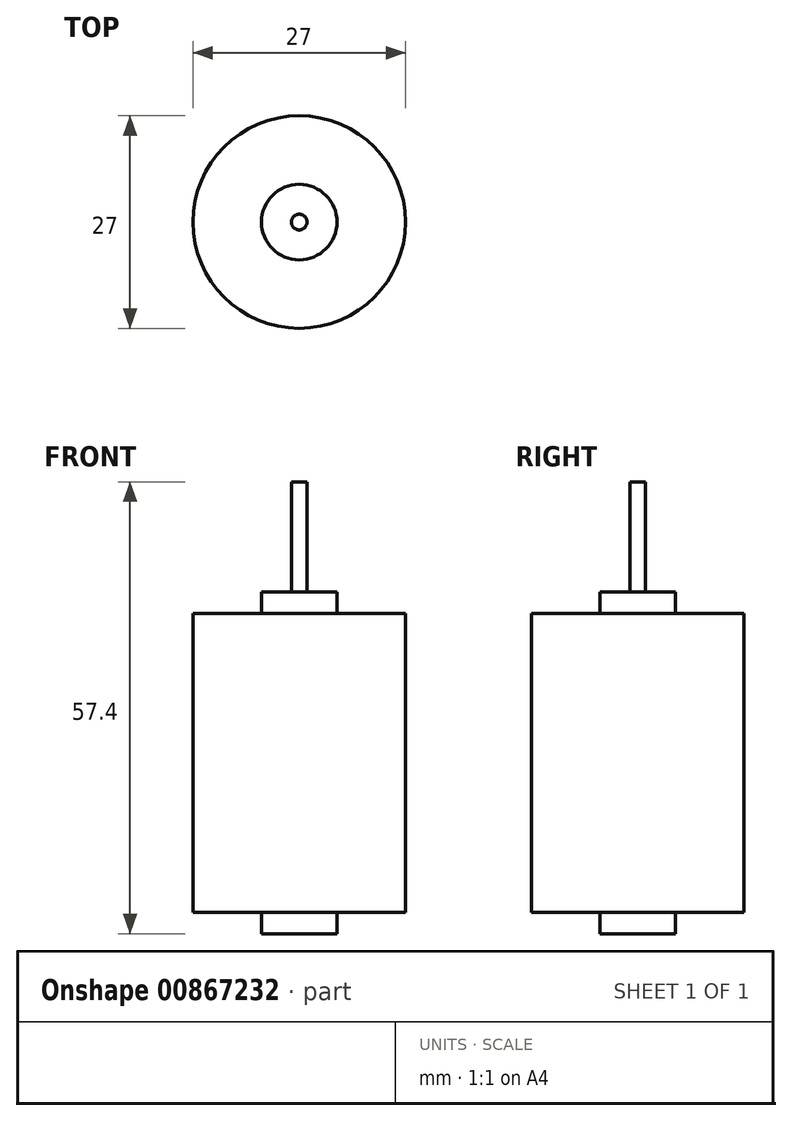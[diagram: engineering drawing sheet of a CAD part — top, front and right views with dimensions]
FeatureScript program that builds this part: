
annotation { "Feature Type Name" : "Feature", "Feature Type Description" : "" }
export const myFeature = defineFeature(function(context is Context, id is Id, definition is map)
    precondition{}
    {
        {
            var Q0;
            Q0=qCreatedBy(makeId("Right.planeOp"),FACE);
            var sketch = newSketch(context, id + "F0", { "sketchPlane" : qUnion([Q0])});
            skLineSegment(sketch, "E0", {"start": v(-56.5, 39.4) * mm, "end": v(-56.5, -18.04) * mm});
            skLineSegment(sketch, "E1", {"start": v(-56.5, 39.4) * mm, "end": v(-55.5, 39.4) * mm});
            skLineSegment(sketch, "E2", {"start": v(-55.5, 39.4) * mm, "end": v(-55.5, 25.4) * mm});
            skLineSegment(sketch, "E3", {"start": v(-55.5, 25.4) * mm, "end": v(-51.7, 25.4) * mm});
            skLineSegment(sketch, "E4", {"start": v(-51.7, 25.4) * mm, "end": v(-51.7, 22.7) * mm});
            skLineSegment(sketch, "E5", {"start": v(-51.7, 22.7) * mm, "end": v(-43, 22.7) * mm});
            skLineSegment(sketch, "E6", {"start": v(-43, 22.7) * mm, "end": v(-43, -15.3) * mm});
            skLineSegment(sketch, "E7", {"start": v(-43, -15.3) * mm, "end": v(-51.7, -15.3) * mm});
            skLineSegment(sketch, "E8", {"start": v(-51.7, -15.3) * mm, "end": v(-51.7, -18) * mm});
            skLineSegment(sketch, "E9", {"start": v(-51.7, -18) * mm, "end": v(-56.5, -18) * mm});
            skSolve(sketch);
        }
        {
            var Q0;
            {var subQ0=sQuery(id+"F0.wireOp",EDGE,"E1");Q0=makeQuery(id+"F0.imprint","IMPRINT",FACE,{"disambiguationData":[TD([[makeQuery(id+"F0.imprint","IMPRINT",EDGE,{"derivedFrom":subQ0}),-1.0]])]});}
            var Q1;
            Q1=sQuery(id+"F0.wireOp",EDGE,"E0");
            revolve(context, id + "F1", {"surfaceOperationType" : NewSurfaceOperationType.NEW, "entities" : qUnion([Q0]), "axis" : qUnion([Q1]), "revolveType" : RevolveType.FULL});
        }
        {
            var Q0;
            Q0=qCreatedBy(makeId("Right.planeOp"),FACE);
            cPlane(context, id + "F2", {"entities" : qUnion([Q0]), "cplaneType" : CPlaneType.OFFSET, "offset" : 25 * mm, "oppositeDirection" : true, "width" : 150 * mm, "height" : 150 * mm});
        }
        {
            var Q0;
            Q0=qCreatedBy(id+"F2.planeOp",FACE);
            cPlane(context, id + "F3", {"entities" : qUnion([Q0]), "cplaneType" : CPlaneType.OFFSET, "offset" : 25 * mm, "oppositeDirection" : true, "width" : 150 * mm, "height" : 150 * mm});
        }
    });
